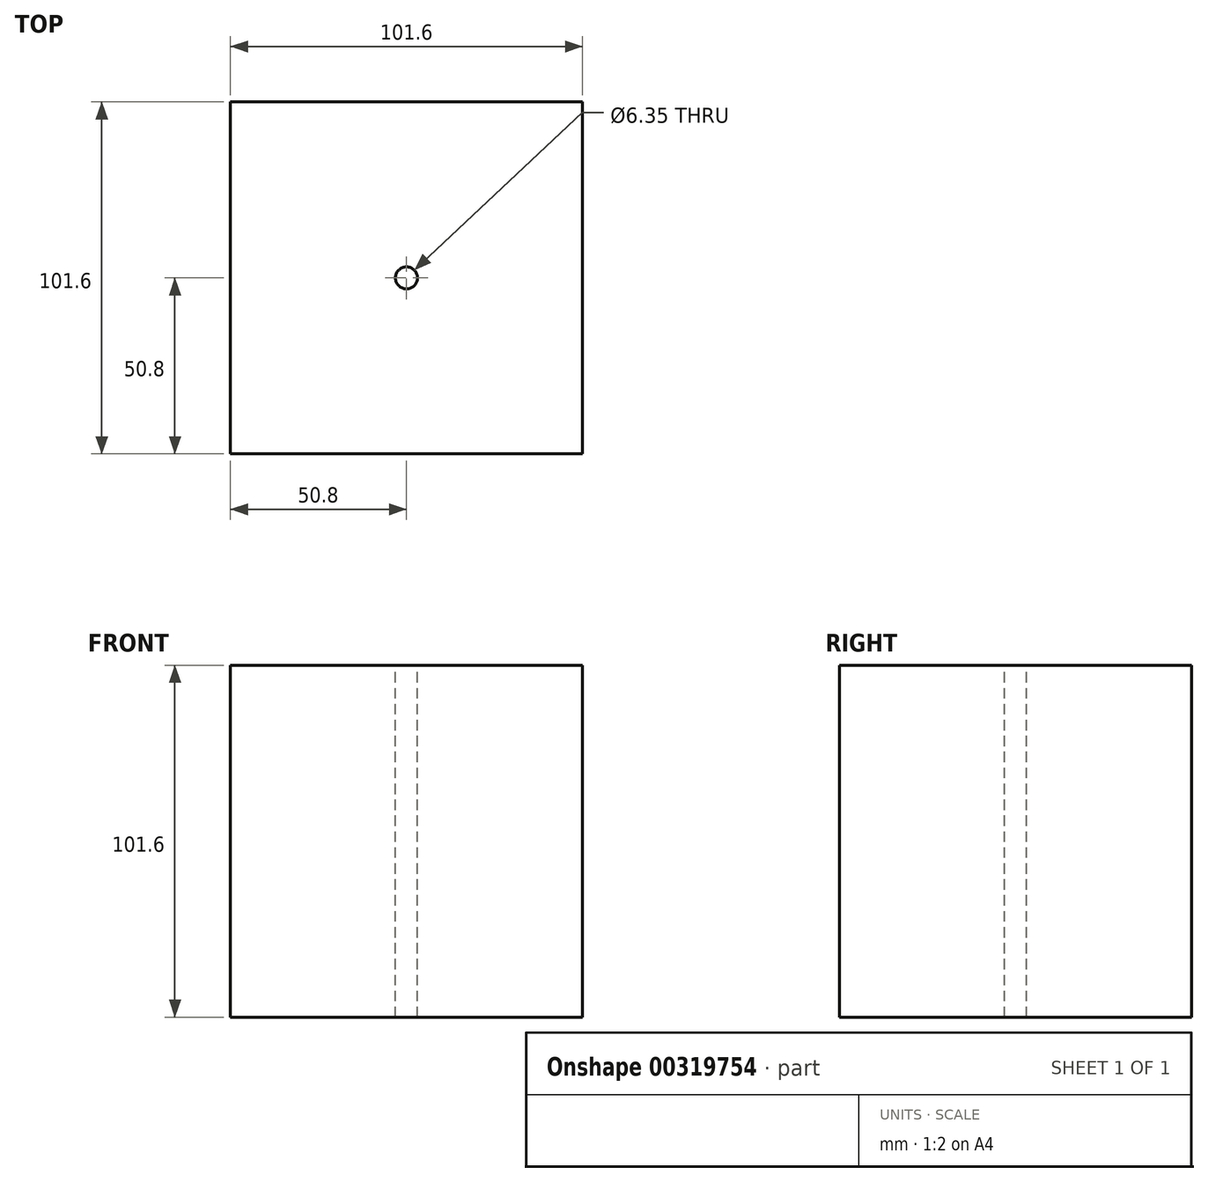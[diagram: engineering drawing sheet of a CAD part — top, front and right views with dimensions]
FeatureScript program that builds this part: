
annotation { "Feature Type Name" : "Feature", "Feature Type Description" : "" }
export const myFeature = defineFeature(function(context is Context, id is Id, definition is map)
    precondition{}
    {
        {
            var Q0;
            Q0=qCreatedBy(makeId("Front.planeOp"),FACE);
            var sketch = newSketch(context, id + "F0", { "sketchPlane" : qUnion([Q0])});
            skLineSegment(sketch, "E0.bottom", {"start": v(-50.8, 50.8) * mm, "end": v(50.8, 50.8) * mm});
            skLineSegment(sketch, "E0.top", {"start": v(-50.8, -50.8) * mm, "end": v(50.8, -50.8) * mm});
            skLineSegment(sketch, "E0.left", {"start": v(-50.8, 50.8) * mm, "end": v(-50.8, -50.8) * mm});
            skLineSegment(sketch, "E0.right", {"start": v(50.8, 50.8) * mm, "end": v(50.8, -50.8) * mm});
            skPoint(sketch, "E0.middle", {"position": v(0, 0) * mm});
            skSolve(sketch);
        }
        {
            var Q0;
            Q0 = qSketchRegion(id + "F0", true);
            extrude(context, id + "F1", {"entities" : qUnion([Q0]), "endBound" : BoundingType.SYMMETRIC, "depth" : 101.6 * mm});
        }
        {
            var Q0;
            Q0=makeQuery(id+"F1.opExtrude","SWEPT_FACE",FACE,{"disambiguationData":[OSD([sQuery(id+"F0.wireOp",EDGE,"E0.bottom")])]});
            var sketch = newSketch(context, id + "F2", { "sketchPlane" : qUnion([Q0])});
            skCircle(sketch, "E1", {"center": v(0, 0) * mm, "radius": 12.7 * mm});
            skSolve(sketch);
        }
        {
            var Q0;
            Q0=sQuery(id+"F2.wireOp",VERTEX,"E1.center");
            var Q1;
            Q1=makeQuery(id+"F1.opExtrude","SWEPT_BODY",BODY,{"disambiguationData":[OSD([sQuery(id+"F0.wireOp",EDGE,"E0.bottom"),sQuery(id+"F0.wireOp",EDGE,"E0.top"),sQuery(id+"F0.wireOp",EDGE,"E0.left"),sQuery(id+"F0.wireOp",EDGE,"E0.right")])]});
            hole(context, id + "F3", {"style" : HoleStyle.SIMPLE, "endStyle" : HoleEndStyle.THROUGH, "holeDiameter" : 6.35 * mm, "tappedDepth" : 12.7 * mm, "tapClearance" : 3, "locations" : qUnion([Q0]), "scope" : qUnion([Q1])});
        }
    });
